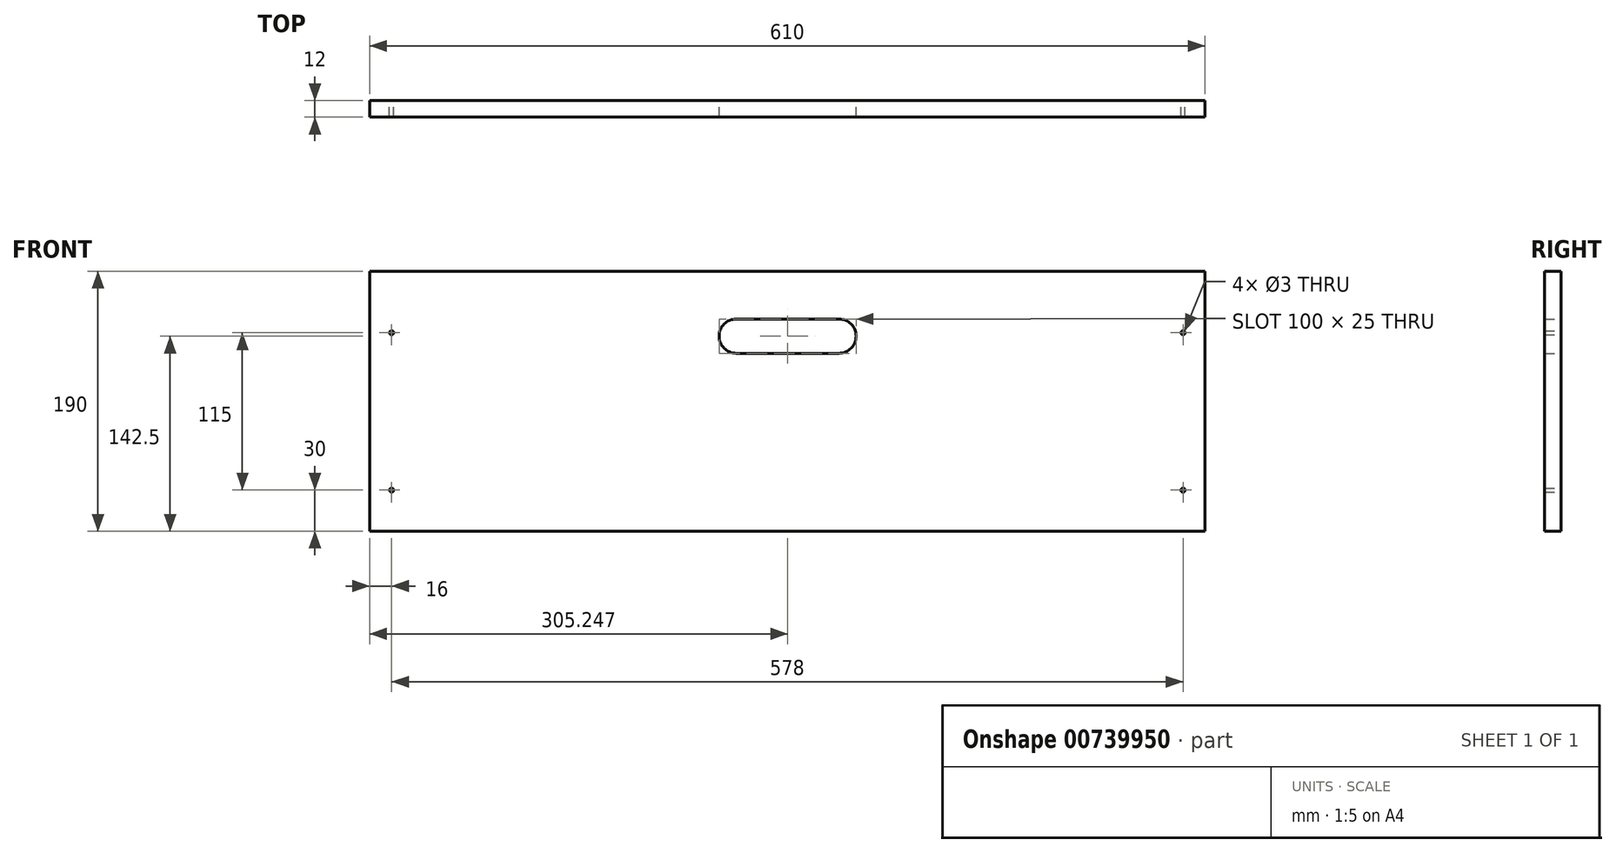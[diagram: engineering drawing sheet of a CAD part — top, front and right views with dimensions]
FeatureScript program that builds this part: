
annotation { "Feature Type Name" : "Feature", "Feature Type Description" : "" }
export const myFeature = defineFeature(function(context is Context, id is Id, definition is map)
    precondition{}
    {
        {
            var Q0;
            Q0=qCreatedBy(makeId("Front.planeOp"),FACE);
            var sketch = newSketch(context, id + "F0", { "sketchPlane" : qUnion([Q0])});
            skLineSegment(sketch, "E0.bottom", {"start": v(305, -95) * mm, "end": v(-305, -95) * mm});
            skLineSegment(sketch, "E0.top", {"start": v(305, 95) * mm, "end": v(-305, 95) * mm});
            skLineSegment(sketch, "E0.left", {"start": v(305, -95) * mm, "end": v(305, 95) * mm});
            skLineSegment(sketch, "E0.right", {"start": v(-305, -95) * mm, "end": v(-305, 95) * mm});
            skPoint(sketch, "E0.middle", {"position": v(0, 0) * mm});
            skLineSegment(sketch, "E1.bottom", {"start": v(37.75, 35) * mm, "end": v(-37.25, 35) * mm});
            skLineSegment(sketch, "E1.top", {"start": v(37.75, 60) * mm, "end": v(-37.25, 60) * mm});
            skPoint(sketch, "E1.middle", {"position": v(0, 47.5) * mm});
            skArc(sketch, "E2", {"start": v(-37.25, 60) * mm, "mid": v(-49.75, 47.5) * mm, "end": v(-37.25, 35) * mm});
            skArc(sketch, "E3", {"start": v(37.75, 35) * mm, "mid": v(50.25, 47.5) * mm, "end": v(37.75, 60) * mm});
            skPoint(sketch, "E4.orphan", {"position": v(-49.42, 60) * mm});
            skPoint(sketch, "E5.orphan", {"position": v(-49.86, 35) * mm});
            skPoint(sketch, "E6.orphan", {"position": v(49.86, 60) * mm});
            skPoint(sketch, "E7.orphan", {"position": v(49.42, 35) * mm});
            skLineSegment(sketch, "E8", {"start": v(-289, 95) * mm, "end": v(-289, -95) * mm, "construction": true});
            skCircle(sketch, "E9", {"center": v(-289, 50) * mm, "radius": 1.5 * mm});
            skCircle(sketch, "E10", {"center": v(-289, -65) * mm, "radius": 1.5 * mm});
            skCircle(sketch, "E11.MirrorC", {"center": v(289, -65) * mm, "radius": 1.5 * mm});
            skCircle(sketch, "E12.MirrorC", {"center": v(289, 50) * mm, "radius": 1.5 * mm});
            skLineSegment(sketch, "E13.MirrorCS", {"start": v(289, 95) * mm, "end": v(289, -95) * mm, "construction": true});
            skSolve(sketch);
        }
        {
            var Q0;
            Q0=makeQuery(id+"F0.imprint","IMPRINT",FACE,{"disambiguationData":[TD([[makeQuery(id+"F0.imprint","IMPRINT",EDGE,{"derivedFrom":sQuery(id+"F0.wireOp",EDGE,"E0.bottom")}),-1.0]])]});
            extrude(context, id + "F1", {"entities" : qUnion([Q0]), "depth" : 12 * mm, "offsetDistance" : 25 * mm, "symmetric" : true});
        }
    });
